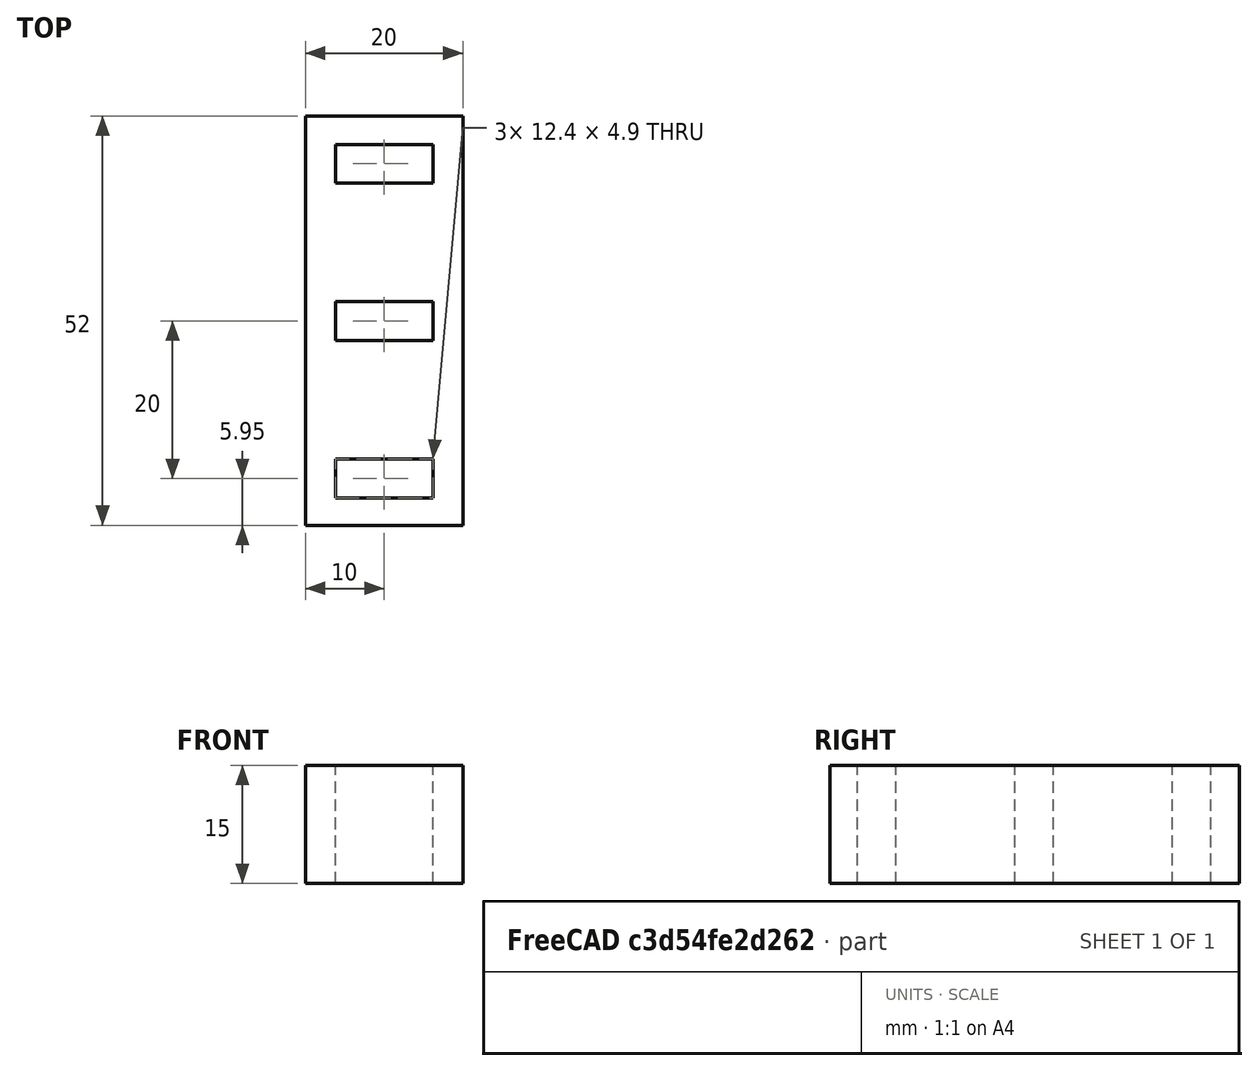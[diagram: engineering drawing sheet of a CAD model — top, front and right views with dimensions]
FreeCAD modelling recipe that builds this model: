
FCSTD DOCUMENT  (FreeCAD 0.20R29410 (Git))
Label: portapendrives
License: Creative Commons Attribution
LicenseURL: http://creativecommons.org/licenses/by/4.0/
objects: Part::Box×4, Part::Cut×3
note: 7 computed .brp shape members not serialized (recipe doc carries the construction recipe); baked Part::Feature solids carry a one-line shape summary decoded from their .brp

FEATURE [Part::Box] Box  label="Cubo"
  AttacherType = Attacher::AttachEngine3D
  Height = 15
  Length = 20
  Width = 52
FEATURE [Part::Box] Box001  label="Cubo001"
  AttacherType = Attacher::AttachEngine3D
  Height = 15
  Length = 12.4
  Placement = pos=(3.8,3.5,0) rot=(0,0,1;0rad)
  Width = 4.9
FEATURE [Part::Cut] Cut
  Base = -> Box
  Refine = true
  Tool = -> Box001
FEATURE [Part::Box] Box002  label="Cubo002"
  AttacherType = Attacher::AttachEngine3D
  Height = 15
  Length = 12.4
  Placement = pos=(3.8,23.5,0) rot=(0,0,1;0rad)
  Width = 4.9
FEATURE [Part::Cut] Cut001
  Base = -> Cut
  Refine = true
  Tool = -> Box002
FEATURE [Part::Box] Box003  label="Cubo003"
  AttacherType = Attacher::AttachEngine3D
  Height = 15
  Length = 12.4
  Placement = pos=(3.8,43.5,0) rot=(0,0,1;0rad)
  Width = 4.9
FEATURE [Part::Cut] Cut002
  Base = -> Cut001
  Refine = true
  Tool = -> Box003
